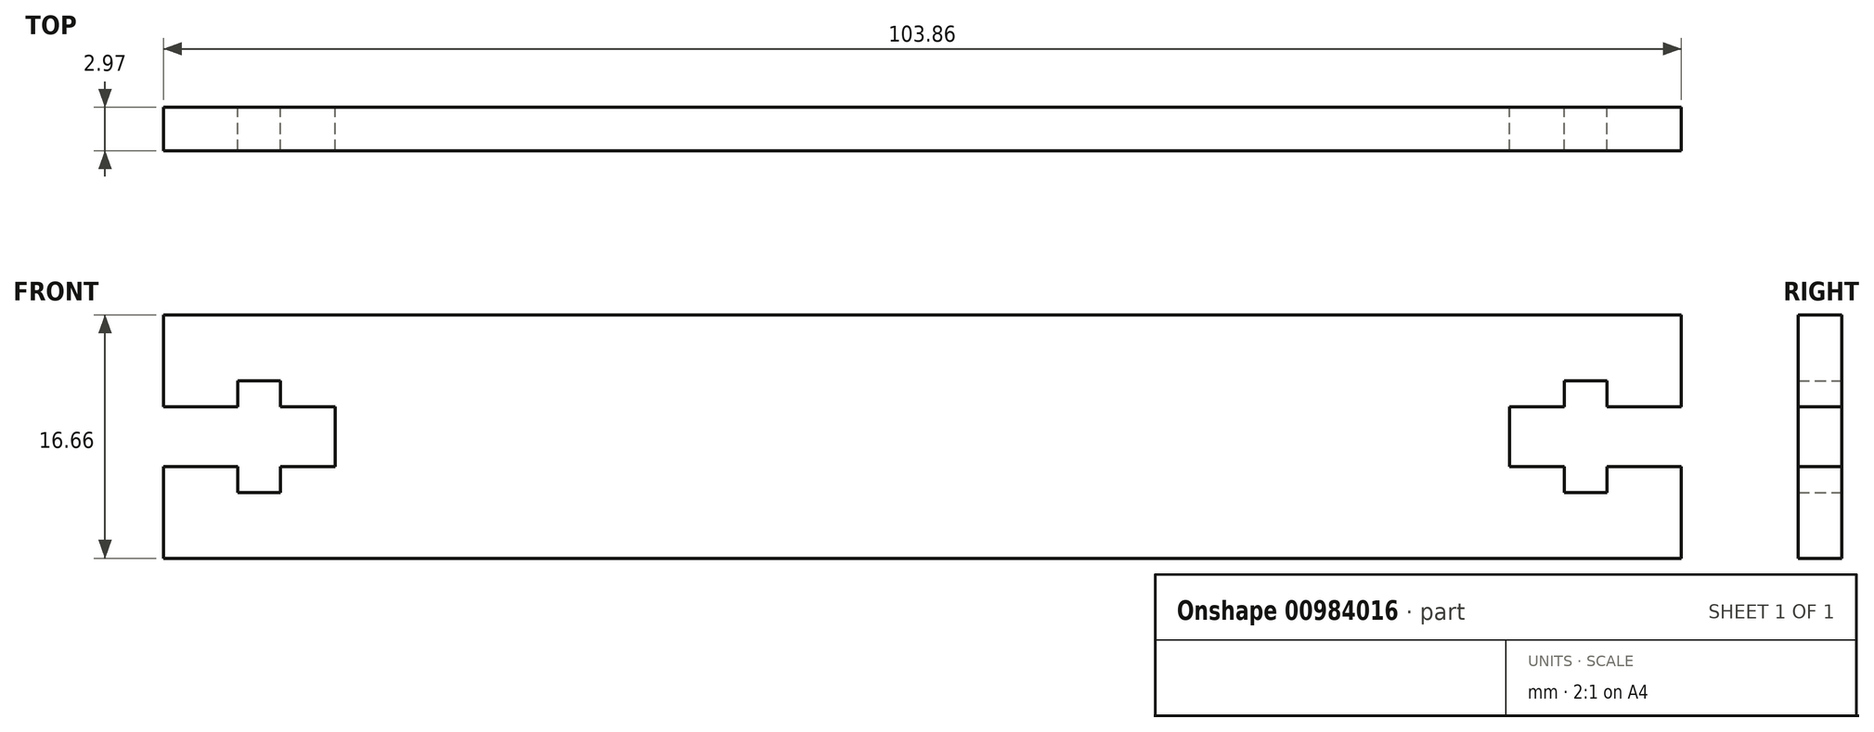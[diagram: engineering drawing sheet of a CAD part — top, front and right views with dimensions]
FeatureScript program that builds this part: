
annotation { "Feature Type Name" : "Feature", "Feature Type Description" : "" }
export const myFeature = defineFeature(function(context is Context, id is Id, definition is map)
    precondition{}
    {
        {
            var Q0;
            Q0=qCreatedBy(makeId("Front.planeOp"),FACE);
            var sketch = newSketch(context, id + "F0", { "sketchPlane" : qUnion([Q0])});
            skLineSegment(sketch, "E0", {"start": v(-57.97, 37.74) * mm, "end": v(50.46, 37.74) * mm});
            skLineSegment(sketch, "E1", {"start": v(-57.97, 21.08) * mm, "end": v(50.46, 21.08) * mm});
            skPoint(sketch, "E2.startSnap0", {"position": v(-62.54, 29.4) * mm});
            skPoint(sketch, "E2.start.orphan", {"position": v(-57.97, 29.4) * mm});
            skLineSegment(sketch, "E3", {"start": v(-57.97, 37.74) * mm, "end": v(-57.97, 31.47) * mm});
            skLineSegment(sketch, "E4", {"start": v(-57.97, 21.08) * mm, "end": v(-57.97, 27.35) * mm});
            skPoint(sketch, "E5.end.orphan", {"position": v(-62.54, 21.08) * mm});
            skPoint(sketch, "E6.orphan", {"position": v(-62.54, 37.74) * mm});
            skPoint(sketch, "E7.end.orphan", {"position": v(-57.97, 43.63) * mm});
            skPoint(sketch, "E7.start.orphan", {"position": v(-62.54, 43.63) * mm});
            skLineSegment(sketch, "E8", {"start": v(-57.97, 27.35) * mm, "end": v(-52.9, 27.35) * mm});
            skLineSegment(sketch, "E9", {"start": v(-57.97, 31.47) * mm, "end": v(-52.9, 31.47) * mm});
            skLineSegment(sketch, "E10", {"start": v(-52.9, 27.35) * mm, "end": v(-52.9, 25.57) * mm});
            skLineSegment(sketch, "E11", {"start": v(-52.9, 25.57) * mm, "end": v(-49.96, 25.57) * mm});
            skLineSegment(sketch, "E12", {"start": v(-49.96, 25.57) * mm, "end": v(-49.96, 27.35) * mm});
            skLineSegment(sketch, "E13", {"start": v(-52.9, 31.47) * mm, "end": v(-52.9, 33.24) * mm});
            skLineSegment(sketch, "E14", {"start": v(-52.9, 33.24) * mm, "end": v(-49.96, 33.24) * mm});
            skLineSegment(sketch, "E15", {"start": v(-49.96, 33.24) * mm, "end": v(-49.96, 31.47) * mm});
            skLineSegment(sketch, "E16", {"start": v(-49.96, 31.47) * mm, "end": v(-46.21, 31.47) * mm});
            skLineSegment(sketch, "E17", {"start": v(-46.21, 31.47) * mm, "end": v(-46.21, 27.35) * mm});
            skLineSegment(sketch, "E18", {"start": v(-46.21, 27.35) * mm, "end": v(-49.96, 27.35) * mm});
            skLineSegment(sketch, "E19", {"start": v(-3.76, 37.74) * mm, "end": v(-3.76, 21.08) * mm, "construction": true});
            skPoint(sketch, "E20.MirrorP", {"position": v(50.46, 29.4) * mm});
            skLineSegment(sketch, "E21", {"start": v(-62.54, 21.08) * mm, "end": v(-57.97, 21.08) * mm});
            skLineSegment(sketch, "E22", {"start": v(-62.54, 37.74) * mm, "end": v(-57.97, 37.74) * mm});
            skPoint(sketch, "E23.MirrorP", {"position": v(55.03, 37.74) * mm});
            skLineSegment(sketch, "E24.MirrorCS", {"start": v(50.46, 21.08) * mm, "end": v(-57.97, 21.08) * mm});
            skLineSegment(sketch, "E25.MirrorCS", {"start": v(50.46, 37.74) * mm, "end": v(-57.97, 37.74) * mm});
            skPoint(sketch, "E26.MirrorP", {"position": v(55.03, 21.08) * mm});
            skPoint(sketch, "E27.MirrorP", {"position": v(55.03, 29.4) * mm});
            skLineSegment(sketch, "E28", {"start": v(50.46, 37.74) * mm, "end": v(45.89, 37.74) * mm});
            skLineSegment(sketch, "E29", {"start": v(45.89, 37.74) * mm, "end": v(45.89, 31.47) * mm});
            skLineSegment(sketch, "E30", {"start": v(45.89, 27.35) * mm, "end": v(45.89, 21.08) * mm});
            skPoint(sketch, "E31.MirrorCS.start.orphan", {"position": v(50.46, 37.74) * mm});
            skPoint(sketch, "E32.MirrorCS.end.orphan", {"position": v(50.46, 31.47) * mm});
            skPoint(sketch, "E33.MirrorCS.start.orphan", {"position": v(50.46, 21.08) * mm});
            skPoint(sketch, "E34.MirrorCS.end.orphan", {"position": v(50.46, 27.35) * mm});
            skLineSegment(sketch, "E35", {"start": v(45.89, 27.35) * mm, "end": v(40.8, 27.35) * mm});
            skLineSegment(sketch, "E36", {"start": v(45.89, 31.47) * mm, "end": v(40.8, 31.47) * mm});
            skLineSegment(sketch, "E37", {"start": v(40.8, 31.47) * mm, "end": v(40.8, 33.24) * mm});
            skLineSegment(sketch, "E38", {"start": v(40.8, 33.24) * mm, "end": v(37.89, 33.24) * mm});
            skLineSegment(sketch, "E39", {"start": v(37.89, 33.24) * mm, "end": v(37.89, 31.47) * mm});
            skLineSegment(sketch, "E40", {"start": v(40.8, 27.35) * mm, "end": v(40.8, 25.57) * mm});
            skLineSegment(sketch, "E41", {"start": v(40.8, 25.57) * mm, "end": v(37.89, 25.57) * mm});
            skLineSegment(sketch, "E42", {"start": v(37.89, 25.57) * mm, "end": v(37.89, 27.35) * mm});
            skLineSegment(sketch, "E43", {"start": v(37.89, 31.47) * mm, "end": v(34.13, 31.47) * mm});
            skLineSegment(sketch, "E44", {"start": v(34.13, 31.47) * mm, "end": v(34.13, 27.35) * mm});
            skLineSegment(sketch, "E45", {"start": v(34.13, 27.35) * mm, "end": v(37.89, 27.35) * mm});
            skSolve(sketch);
        }
        {
            var Q0;
            Q0=makeQuery(id+"F0.imprint","IMPRINT",FACE,{"disambiguationData":[TD([[makeQuery(id+"F0.imprint","IMPRINT",EDGE,{"derivedFrom":sQuery(id+"F0.wireOp",EDGE,"E3")}),1.0]])]});
            extrude(context, id + "F1", {"entities" : qUnion([Q0]), "depth" : 2.97 * mm, "offsetDistance" : 25.4 * mm});
        }
    });
